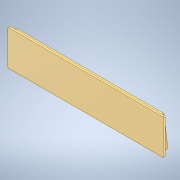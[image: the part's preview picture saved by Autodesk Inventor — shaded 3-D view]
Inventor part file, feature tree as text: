
AUTODESK INVENTOR PART (.ipt)
format: ipt  version: 2020 (Build 240168000, 168)  size: 116,224 bytes
history: mixed  units: mm
features: fillet x1, imported_body x1
ambient origin geometry x8: Origin, YZ Plane, XZ Plane, XY Plane, X Axis, Y Axis, Z Axis, Center Point
bodies: Solid1 (imported_parasolid)
feature tree (2):
  fillet  "Fillet1"  [1 undecoded]
  imported_body  NMx_Import_Brep_tag  [imported B-rep: ~19 faces, bbox_mm=[264.0, 60.0, 14.605935]]
note: 1 required parameter value undecoded (feature->parameter linkage not recoverable at this tier; creation-order binding heuristic only, values carry confidence <= 0.55)
